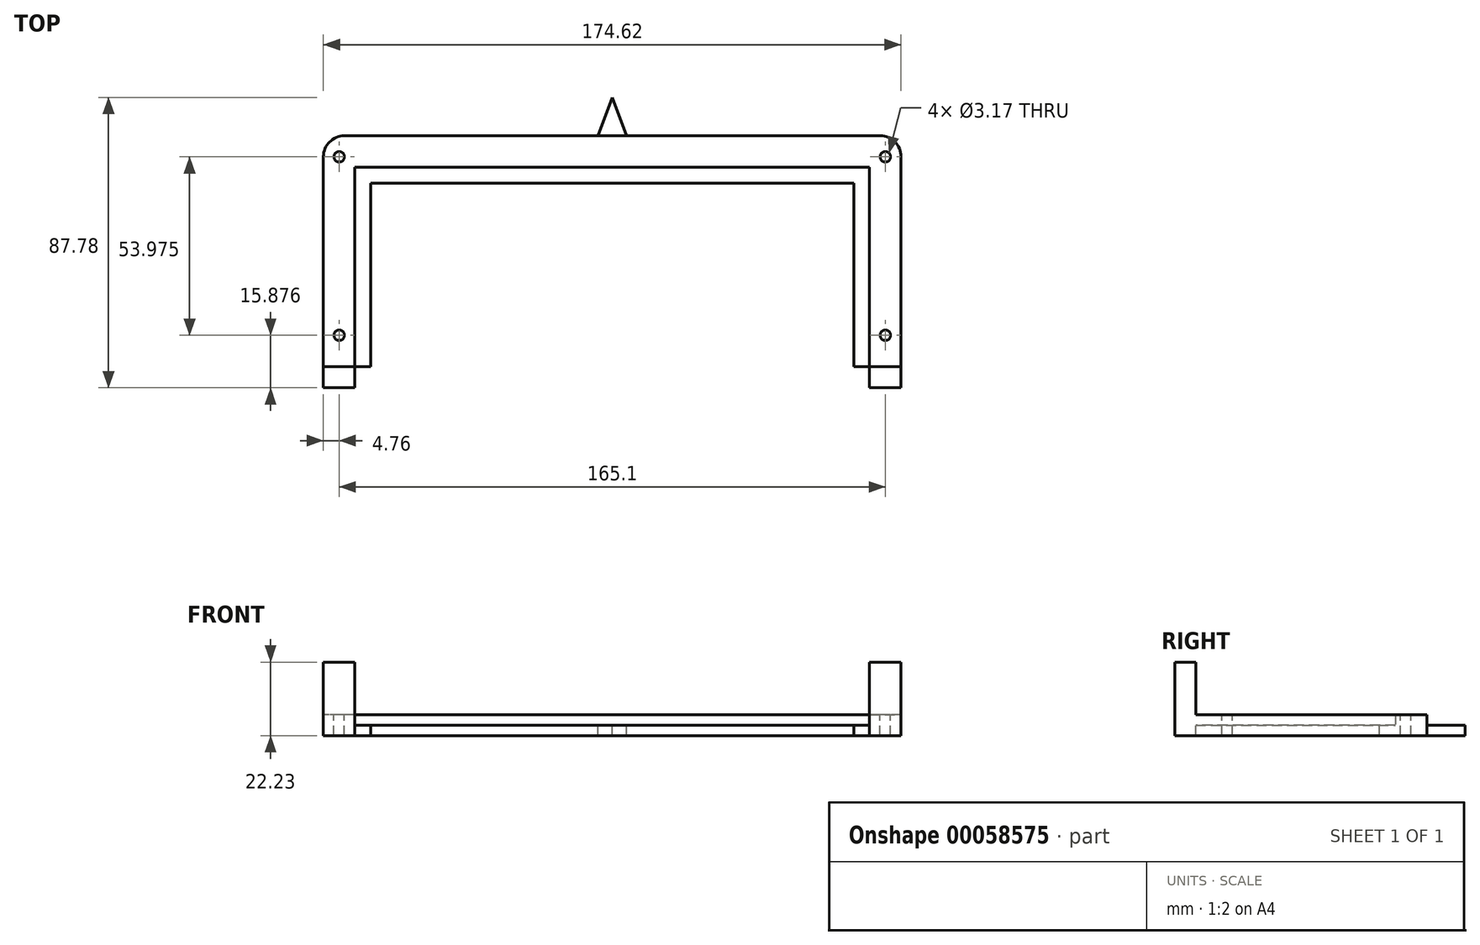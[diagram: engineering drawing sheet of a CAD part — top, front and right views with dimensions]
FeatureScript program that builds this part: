
annotation { "Feature Type Name" : "Feature", "Feature Type Description" : "" }
export const myFeature = defineFeature(function(context is Context, id is Id, definition is map)
    precondition{}
    {
        {
            var Q0;
            Q0=qCreatedBy(makeId("Top.planeOp"),FACE);
            var sketch = newSketch(context, id + "F0", { "sketchPlane" : qUnion([Q0])});
            skLineSegment(sketch, "E0.rect.top", {"start": v(73.03, 26.2) * mm, "end": v(-73.03, 26.2) * mm});
            skLineSegment(sketch, "E0.rect.left", {"start": v(73.03, -26.2) * mm, "end": v(73.03, 26.2) * mm});
            skLineSegment(sketch, "E0.rect.right", {"start": v(-73.03, -26.2) * mm, "end": v(-73.03, 26.2) * mm});
            skPoint(sketch, "E0.rect.middle", {"position": v(0, 0) * mm});
            skLineSegment(sketch, "E1", {"start": v(87.31, -26.2) * mm, "end": v(87.31, 34.13) * mm});
            skLineSegment(sketch, "E2", {"start": v(80.96, 40.48) * mm, "end": v(9.53, 40.48) * mm});
            skLineSegment(sketch, "E3", {"start": v(-87.31, 34.13) * mm, "end": v(-87.31, -26.2) * mm});
            skLineSegment(sketch, "E4", {"start": v(-77.79, -26.2) * mm, "end": v(-77.79, 30.96) * mm});
            skLineSegment(sketch, "E5", {"start": v(-77.79, 30.96) * mm, "end": v(77.79, 30.96) * mm});
            skLineSegment(sketch, "E6", {"start": v(77.79, 30.96) * mm, "end": v(77.79, -26.2) * mm});
            skCircle(sketch, "E7", {"center": v(82.55, -19.84) * mm, "radius": 1.59 * mm});
            skCircle(sketch, "E8", {"center": v(82.55, 34.13) * mm, "radius": 1.59 * mm});
            skCircle(sketch, "E9", {"center": v(-82.55, 34.13) * mm, "radius": 1.59 * mm});
            skCircle(sketch, "E10", {"center": v(-82.55, -19.84) * mm, "radius": 1.59 * mm});
            skLineSegment(sketch, "E11", {"start": v(-87.31, -26.2) * mm, "end": v(-87.31, -32.54) * mm});
            skLineSegment(sketch, "E12", {"start": v(-77.79, -32.54) * mm, "end": v(-77.79, -26.2) * mm});
            skLineSegment(sketch, "E13", {"start": v(77.79, -26.2) * mm, "end": v(77.79, -32.54) * mm});
            skLineSegment(sketch, "E14", {"start": v(87.31, -32.54) * mm, "end": v(87.31, -26.2) * mm});
            skPoint(sketch, "E15.visualSharp", {"position": v(87.31, 40.48) * mm});
            skArc(sketch, "E15.filletArc", {"start": v(87.31, 34.13) * mm, "mid": v(85.45, 38.62) * mm, "end": v(80.96, 40.48) * mm});
            skPoint(sketch, "E16.visualSharp", {"position": v(-87.31, 40.48) * mm});
            skArc(sketch, "E16.filletArc", {"start": v(-80.96, 40.48) * mm, "mid": v(-85.45, 38.62) * mm, "end": v(-87.31, 34.13) * mm});
            skPoint(sketch, "E17", {"position": v(0, 40.48) * mm});
            skLineSegment(sketch, "E18.trimOffspring", {"start": v(-9.53, 40.48) * mm, "end": v(-80.96, 40.48) * mm});
            skLineSegment(sketch, "E19.trimOffspring", {"start": v(7.94, 40.48) * mm, "end": v(-1.59, 40.48) * mm});
            skLineSegment(sketch, "E20", {"start": v(-9.53, 40.48) * mm, "end": v(-1.59, 40.48) * mm});
            skLineSegment(sketch, "E21", {"start": v(7.94, 40.48) * mm, "end": v(9.53, 40.48) * mm});
            skLineSegment(sketch, "E22", {"start": v(-73.03, -26.2) * mm, "end": v(-73.03, -29.37) * mm});
            skLineSegment(sketch, "E23", {"start": v(-73.03, -29.37) * mm, "end": v(-77.79, -29.37) * mm});
            skLineSegment(sketch, "E24", {"start": v(-77.79, -32.54) * mm, "end": v(-77.79, -35.72) * mm});
            skLineSegment(sketch, "E25", {"start": v(-77.79, -35.72) * mm, "end": v(-87.31, -35.72) * mm});
            skLineSegment(sketch, "E26", {"start": v(-87.31, -35.72) * mm, "end": v(-87.31, -32.54) * mm});
            skLineSegment(sketch, "E27", {"start": v(-77.79, -29.37) * mm, "end": v(-87.31, -29.37) * mm});
            skLineSegment(sketch, "E28", {"start": v(77.79, -32.54) * mm, "end": v(77.79, -35.72) * mm});
            skLineSegment(sketch, "E29", {"start": v(77.79, -35.72) * mm, "end": v(87.31, -35.72) * mm});
            skLineSegment(sketch, "E30", {"start": v(87.31, -35.72) * mm, "end": v(87.31, -32.54) * mm});
            skLineSegment(sketch, "E31", {"start": v(73.03, -29.37) * mm, "end": v(73.03, -26.2) * mm});
            skLineSegment(sketch, "E32", {"start": v(73.03, -29.37) * mm, "end": v(77.79, -29.37) * mm});
            skLineSegment(sketch, "E33", {"start": v(77.79, -29.37) * mm, "end": v(87.31, -29.37) * mm});
            skPoint(sketch, "E34.start.orphan", {"position": v(3.17, 65.88) * mm});
            skLineSegment(sketch, "E35", {"start": v(0, 65.88) * mm, "end": v(-9.53, 40.48) * mm});
            skLineSegment(sketch, "E36", {"start": v(0, 65.88) * mm, "end": v(9.53, 40.48) * mm});
            skLineSegment(sketch, "E37", {"start": v(0, 52.06) * mm, "end": v(-4.34, 40.48) * mm});
            skLineSegment(sketch, "E38", {"start": v(0, 52.06) * mm, "end": v(4.34, 40.48) * mm});
            skLineSegment(sketch, "E39", {"start": v(4.34, 40.48) * mm, "end": v(-4.34, 40.48) * mm});
            skSolve(sketch);
        }
        {
            var Q0;
            Q0=makeQuery(id+"F0.imprint","IMPRINT",FACE,{"disambiguationData":[TD([[makeQuery(id+"F0.imprint","IMPRINT",EDGE,{"derivedFrom":sQuery(id+"F0.wireOp",EDGE,"E0.rect.top")}),-1.0]])]});
            var Q1;
            {var subQ0=sQuery(id+"F0.wireOp",EDGE,"E11");Q1=makeQuery(id+"F0.imprint","IMPRINT",FACE,{"disambiguationData":[TD([[makeQuery(id+"F0.imprint","IMPRINT",EDGE,{"derivedFrom":subQ0}),1.0]])]});}
            var Q2;
            {var subQ3=sQuery(id+"F0.wireOp",EDGE,"E1");Q2=makeQuery(id+"F0.imprint","IMPRINT",FACE,{"disambiguationData":[TD([[makeQuery(id+"F0.imprint","IMPRINT",EDGE,{"derivedFrom":subQ3}),1.0]])]});}
            var Q3;
            {var subQ2=sQuery(id+"F0.wireOp",EDGE,"E13");Q3=makeQuery(id+"F0.imprint","IMPRINT",FACE,{"disambiguationData":[TD([[makeQuery(id+"F0.imprint","IMPRINT",EDGE,{"derivedFrom":subQ2}),1.0]])]});}
            var Q4;
            Q4=makeQuery(id+"F0.imprint","IMPRINT",FACE,{"disambiguationData":[TD([[makeQuery(id+"F0.imprint","IMPRINT",EDGE,{"derivedFrom":sQuery(id+"F0.wireOp",EDGE,"E34")}),1.0]])]});
            var Q5;
            Q5=makeQuery(id+"F0.imprint","IMPRINT",FACE,{"disambiguationData":[TD([[makeQuery(id+"F0.imprint","IMPRINT",EDGE,{"derivedFrom":sQuery(id+"F0.wireOp",EDGE,"E19.trimOffspring")}),-1.0]])]});
            extrude(context, id + "F1", {"entities" : qUnion([Q0, Q1, Q2, Q3, Q4, Q5]), "oppositeDirection" : true, "depth" : 3.17 * mm});
        }
        {
            var Q0;
            {var subQ3=sQuery(id+"F0.wireOp",EDGE,"E1");Q0=makeQuery(id+"F0.imprint","IMPRINT",FACE,{"disambiguationData":[TD([[makeQuery(id+"F0.imprint","IMPRINT",EDGE,{"derivedFrom":subQ3}),1.0]])]});}
            extrude(context, id + "F2", {"entities" : qUnion([Q0]), "operationType" : NewBodyOperationType.ADD, "depth" : 3.17 * mm});
        }
        {
            var Q0;
            {var subQ0=sQuery(id+"F0.wireOp",EDGE,"E11");Q0=makeQuery(id+"F0.imprint","IMPRINT",FACE,{"disambiguationData":[TD([[makeQuery(id+"F0.imprint","IMPRINT",EDGE,{"derivedFrom":subQ0}),1.0]])]});}
            var Q1;
            {var subQ2=sQuery(id+"F0.wireOp",EDGE,"E13");Q1=makeQuery(id+"F0.imprint","IMPRINT",FACE,{"disambiguationData":[TD([[makeQuery(id+"F0.imprint","IMPRINT",EDGE,{"derivedFrom":subQ2}),1.0]])]});}
            extrude(context, id + "F3", {"entities" : qUnion([Q0, Q1]), "operationType" : NewBodyOperationType.ADD, "depth" : 19.05 * mm});
        }
    });
